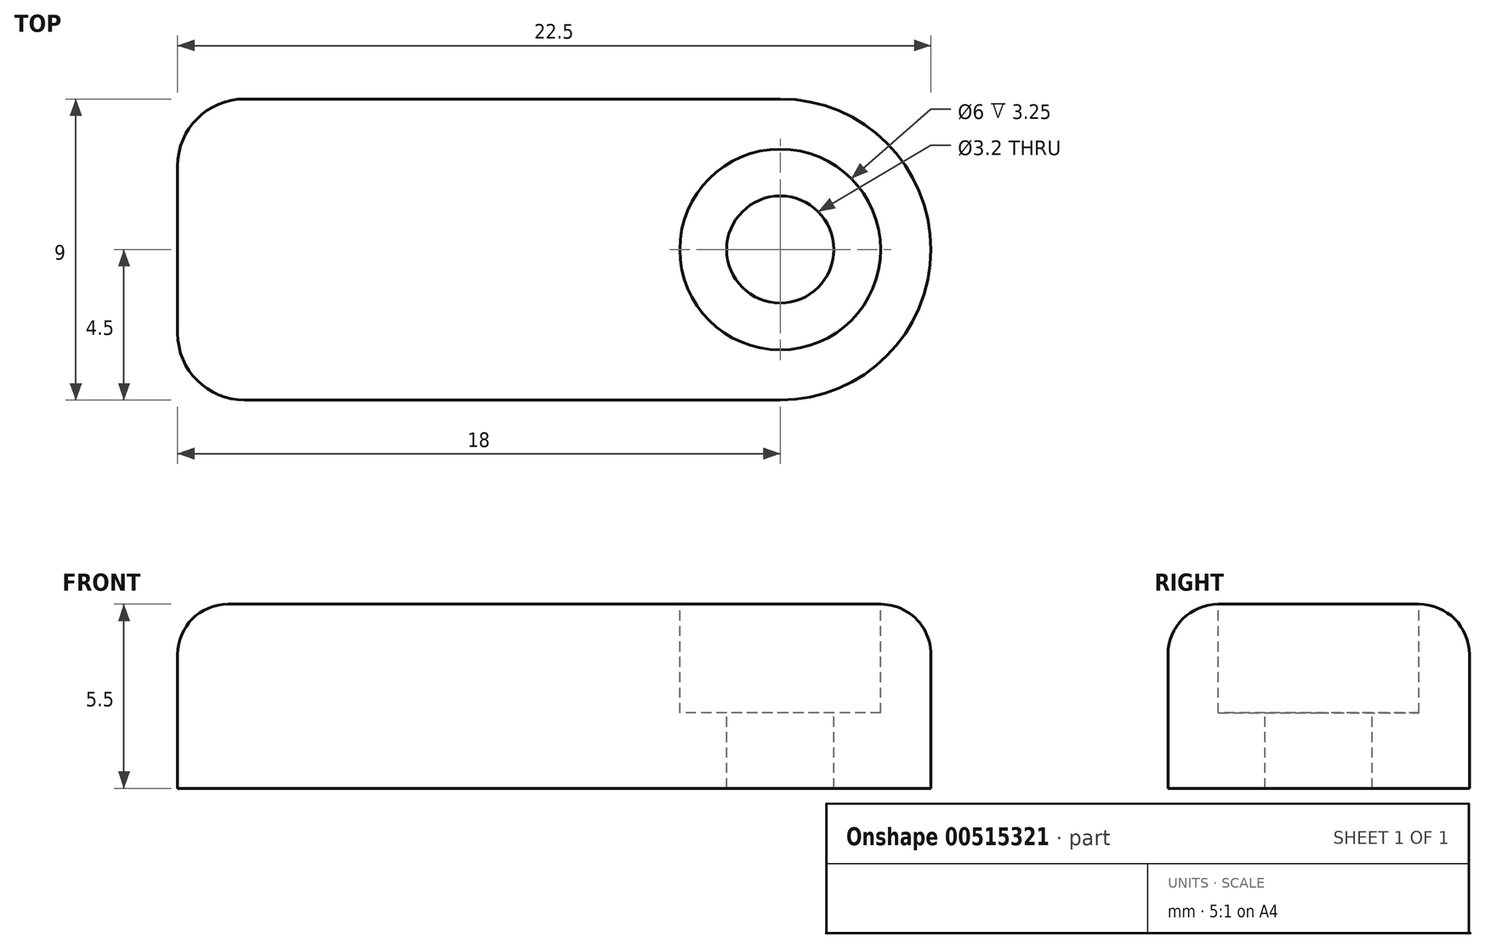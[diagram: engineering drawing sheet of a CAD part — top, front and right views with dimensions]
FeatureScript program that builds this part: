
annotation { "Feature Type Name" : "Feature", "Feature Type Description" : "" }
export const myFeature = defineFeature(function(context is Context, id is Id, definition is map)
    precondition{}
    {
        {
            var Q0;
            Q0=qCreatedBy(makeId("Top.planeOp"),FACE);
            var sketch = newSketch(context, id + "F0", { "sketchPlane" : qUnion([Q0])});
            skLineSegment(sketch, "E0.bottom", {"start": v(-18, 4.5) * mm, "end": v(4.5, 4.5) * mm});
            skLineSegment(sketch, "E0.top", {"start": v(-18, -4.5) * mm, "end": v(4.5, -4.5) * mm});
            skLineSegment(sketch, "E0.left", {"start": v(-18, 4.5) * mm, "end": v(-18, -4.5) * mm});
            skLineSegment(sketch, "E0.right", {"start": v(4.5, 4.5) * mm, "end": v(4.5, -4.5) * mm});
            skSolve(sketch);
        }
        {
            var Q0;
            Q0 = qSketchRegion(id + "F0", true);
            extrude(context, id + "F1", {"entities" : qUnion([Q0]), "depth" : 5.5 * mm, "offsetDistance" : 25 * mm});
        }
        {
            var Q0;
            Q0=makeQuery(id+"F1.opExtrude","CAP_FACE",FACE,{"disambiguationData":[OSD([sQuery(id+"F0.wireOp",EDGE,"E0.bottom"),sQuery(id+"F0.wireOp",EDGE,"E0.top"),sQuery(id+"F0.wireOp",EDGE,"E0.left"),sQuery(id+"F0.wireOp",EDGE,"E0.right")])],"isStart":false});
            var sketch = newSketch(context, id + "F2", { "sketchPlane" : qUnion([Q0])});
            skCircle(sketch, "E1", {"center": v(0, 0) * mm, "radius": 3 * mm});
            skSolve(sketch);
        }
        {
            var Q0;
            Q0 = qSketchRegion(id + "F2", true);
            extrude(context, id + "F3", {"entities" : qUnion([Q0]), "operationType" : NewBodyOperationType.REMOVE, "oppositeDirection" : true, "depth" : 3.25 * mm, "offsetDistance" : 25 * mm});
        }
        {
            var Q0;
            Q0=makeQuery(id+"F3.boolean.opBoolean","COPY",FACE,{"derivedFrom":makeQuery(id+"F3.opExtrude","CAP_FACE",FACE,{"disambiguationData":[OSD([sQuery(id+"F2.wireOp",EDGE,"E1")])],"isStart":false})});
            var sketch = newSketch(context, id + "F4", { "sketchPlane" : qUnion([Q0])});
            skCircle(sketch, "E2", {"center": v(0, 0) * mm, "radius": 1.6 * mm});
            skSolve(sketch);
        }
        {
            var Q0;
            Q0 = qSketchRegion(id + "F4", true);
            extrude(context, id + "F5", {"entities" : qUnion([Q0]), "operationType" : NewBodyOperationType.REMOVE, "oppositeDirection" : true, "depth" : 2.5 * mm, "offsetDistance" : 25 * mm});
        }
        {
            var Q0;
            Q0=makeQuery(id+"F1.opExtrude","SWEPT_EDGE",EDGE,{"disambiguationData":[OSD([sQuery(id+"F0.wireOp",EDGE,"E0.top"),sQuery(id+"F0.wireOp",EDGE,"E0.right")])]});
            var Q1;
            Q1=makeQuery(id+"F1.opExtrude","SWEPT_EDGE",EDGE,{"disambiguationData":[OSD([sQuery(id+"F0.wireOp",EDGE,"E0.bottom"),sQuery(id+"F0.wireOp",EDGE,"E0.right")])]});
            fillet(context, id + "F6", {"entities" : qUnion([Q0, Q1]), "radius" : 4.5 * mm, "tangentPropagation" : true, "allowEdgeOverflow" : false});
        }
        {
            var Q0;
            Q0=makeQuery(id+"F1.opExtrude","SWEPT_EDGE",EDGE,{"disambiguationData":[OSD([sQuery(id+"F0.wireOp",EDGE,"E0.bottom"),sQuery(id+"F0.wireOp",EDGE,"E0.left")])]});
            var Q1;
            Q1=makeQuery(id+"F1.opExtrude","SWEPT_EDGE",EDGE,{"disambiguationData":[OSD([sQuery(id+"F0.wireOp",EDGE,"E0.top"),sQuery(id+"F0.wireOp",EDGE,"E0.left")])]});
            fillet(context, id + "F7", {"entities" : qUnion([Q0, Q1]), "radius" : 2 * mm, "tangentPropagation" : true, "allowEdgeOverflow" : false});
        }
        {
            var Q0;
            Q0=makeQuery(id+"F1.opExtrude","CAP_EDGE",EDGE,{"disambiguationData":[OSD([sQuery(id+"F0.wireOp",EDGE,"E0.top")])],"isStart":false});
            fillet(context, id + "F8", {"entities" : qUnion([Q0]), "radius" : 1.5 * mm, "tangentPropagation" : true, "allowEdgeOverflow" : false});
        }
    });
